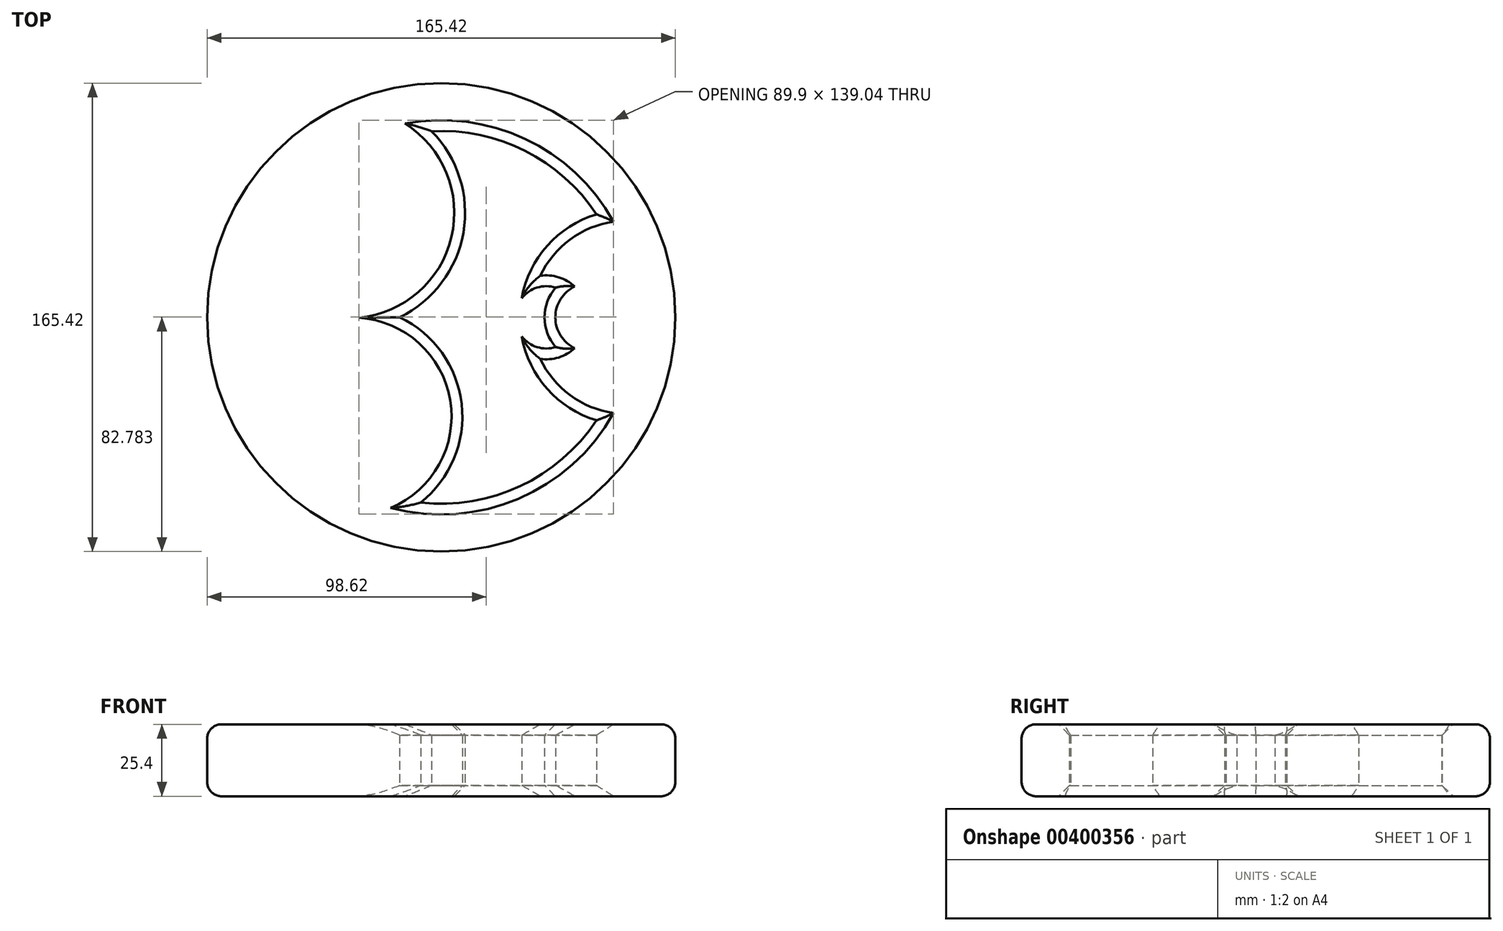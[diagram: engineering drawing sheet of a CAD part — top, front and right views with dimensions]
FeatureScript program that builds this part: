
annotation { "Feature Type Name" : "Feature", "Feature Type Description" : "" }
export const myFeature = defineFeature(function(context is Context, id is Id, definition is map)
    precondition{}
    {
        {
            var Q0;
            Q0=qCreatedBy(makeId("Top.planeOp"),FACE);
            var sketch = newSketch(context, id + "F0", { "sketchPlane" : qUnion([Q0])});
            skArc(sketch, "E0", {"start": v(54.85, 36.37) * mm, "mid": v(29.62, 58.77) * mm, "end": v(-3.4, 65.73) * mm});
            skArc(sketch, "E1", {"start": v(54.85, 36.37) * mm, "mid": v(37.46, 25.29) * mm, "end": v(28.43, 6.75) * mm});
            skArc(sketch, "E2", {"start": v(-7.25, -65.41) * mm, "mid": v(7.2, -30.64) * mm, "end": v(-14.7, 0) * mm});
            skArc(sketch, "E3", {"start": v(-14.7, 0) * mm, "mid": v(7.82, 29.96) * mm, "end": v(-3.4, 65.73) * mm});
            skArc(sketch, "E4", {"start": v(40.45, 10.5) * mm, "mid": v(33.85, 10.5) * mm, "end": v(28.43, 6.75) * mm});
            skArc(sketch, "E5", {"start": v(40.45, 10.5) * mm, "mid": v(36.48, 0) * mm, "end": v(40.45, -10.5) * mm});
            skArc(sketch, "E6.trimOffspring", {"start": v(28.43, -6.75) * mm, "mid": v(37.46, -25.29) * mm, "end": v(54.85, -36.37) * mm});
            skArc(sketch, "E7.trimOffspring", {"start": v(28.43, -6.75) * mm, "mid": v(33.85, -10.5) * mm, "end": v(40.45, -10.5) * mm});
            skArc(sketch, "E8.trimOffspring", {"start": v(-7.25, -65.41) * mm, "mid": v(27.88, -59.62) * mm, "end": v(54.85, -36.37) * mm});
            skCircle(sketch, "E9", {"center": v(0, 0) * mm, "radius": 82.7 * mm});
            skSolve(sketch);
        }
        {
            var Q0;
            {var subQ1=sQuery(id+"F0.wireOp",EDGE,"E0");Q0=makeQuery(id+"F0.imprint","IMPRINT",FACE,{"disambiguationData":[TD([[makeQuery(id+"F0.imprint","IMPRINT",EDGE,{"derivedFrom":subQ1}),-1.0]])]});}
            extrude(context, id + "F1", {"entities" : qUnion([Q0]), "depth" : 25.4 * mm});
        }
        {
            var Q0;
            Q0=makeQuery(id+"F1.opExtrude","CAP_EDGE",EDGE,{"disambiguationData":[OSD([sQuery(id+"F0.wireOp",EDGE,"E9")])],"isStart":false});
            fillet(context, id + "F2", {"entities" : qUnion([Q0]), "radius" : 5.08 * mm, "tangentPropagation" : true, "allowEdgeOverflow" : false});
        }
        {
            var Q0;
            Q0=makeQuery(id+"F1.opExtrude","CAP_FACE",FACE,{"disambiguationData":[OSD([sQuery(id+"F0.wireOp",EDGE,"E0"),sQuery(id+"F0.wireOp",EDGE,"E1"),sQuery(id+"F0.wireOp",EDGE,"E2"),sQuery(id+"F0.wireOp",EDGE,"E3"),sQuery(id+"F0.wireOp",EDGE,"E4"),sQuery(id+"F0.wireOp",EDGE,"E5"),sQuery(id+"F0.wireOp",EDGE,"E6.trimOffspring"),sQuery(id+"F0.wireOp",EDGE,"E7.trimOffspring"),sQuery(id+"F0.wireOp",EDGE,"E8.trimOffspring"),sQuery(id+"F0.wireOp",EDGE,"E9")])],"isStart":false});
            chamfer(context, id + "F3", {"entities" : qUnion([Q0]), "width" : 3.8 * mm, "tangentPropagation" : true});
        }
        {
            var Q0;
            Q0=makeQuery(id+"F1.opExtrude","CAP_EDGE",EDGE,{"disambiguationData":[OSD([sQuery(id+"F0.wireOp",EDGE,"E1")])],"isStart":true});
            var Q1;
            Q1=makeQuery(id+"F1.opExtrude","CAP_EDGE",EDGE,{"disambiguationData":[OSD([sQuery(id+"F0.wireOp",EDGE,"E0")])],"isStart":true});
            var Q2;
            Q2=makeQuery(id+"F1.opExtrude","CAP_EDGE",EDGE,{"disambiguationData":[OSD([sQuery(id+"F0.wireOp",EDGE,"E3")])],"isStart":true});
            var Q3;
            Q3=makeQuery(id+"F1.opExtrude","CAP_EDGE",EDGE,{"disambiguationData":[OSD([sQuery(id+"F0.wireOp",EDGE,"E4")])],"isStart":true});
            var Q4;
            Q4=makeQuery(id+"F1.opExtrude","CAP_EDGE",EDGE,{"disambiguationData":[OSD([sQuery(id+"F0.wireOp",EDGE,"E5")])],"isStart":true});
            var Q5;
            Q5=makeQuery(id+"F1.opExtrude","CAP_EDGE",EDGE,{"disambiguationData":[OSD([sQuery(id+"F0.wireOp",EDGE,"E7.trimOffspring")])],"isStart":true});
            var Q6;
            Q6=makeQuery(id+"F1.opExtrude","CAP_EDGE",EDGE,{"disambiguationData":[OSD([sQuery(id+"F0.wireOp",EDGE,"E6.trimOffspring")])],"isStart":true});
            var Q7;
            Q7=makeQuery(id+"F1.opExtrude","CAP_EDGE",EDGE,{"disambiguationData":[OSD([sQuery(id+"F0.wireOp",EDGE,"E8.trimOffspring")])],"isStart":true});
            chamfer(context, id + "F4", {"entities" : qUnion([Q0, Q1, Q2, Q3, Q4, Q5, Q6, Q7]), "width" : 3.8 * mm, "tangentPropagation" : true});
        }
        {
            var Q0;
            Q0=makeQuery(id+"F1.opExtrude","CAP_EDGE",EDGE,{"disambiguationData":[OSD([sQuery(id+"F0.wireOp",EDGE,"E9")])],"isStart":true});
            fillet(context, id + "F5", {"entities" : qUnion([Q0]), "radius" : 5.08 * mm, "tangentPropagation" : true, "allowEdgeOverflow" : false});
        }
        {
            var Q0;
            Q0=makeQuery(id+"F1.opExtrude","CAP_EDGE",EDGE,{"disambiguationData":[OSD([sQuery(id+"F0.wireOp",EDGE,"E2")])],"isStart":true});
            chamfer(context, id + "F6", {"entities" : qUnion([Q0]), "width" : 3.8 * mm, "tangentPropagation" : true});
        }
    });
